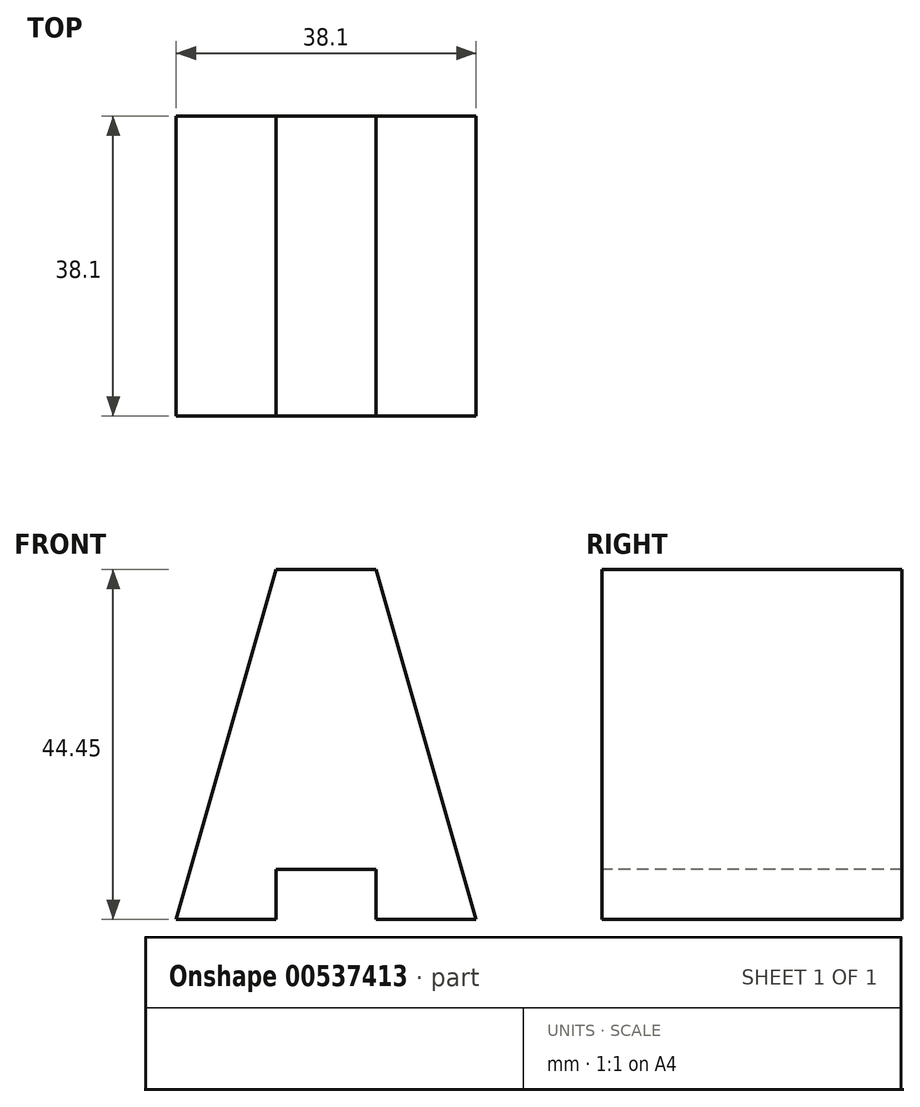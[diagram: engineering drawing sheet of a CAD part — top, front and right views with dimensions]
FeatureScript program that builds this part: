
annotation { "Feature Type Name" : "Feature", "Feature Type Description" : "" }
export const myFeature = defineFeature(function(context is Context, id is Id, definition is map)
    precondition{}
    {
        {
            var Q0;
            Q0=qCreatedBy(makeId("Front.planeOp"),FACE);
            var sketch = newSketch(context, id + "F0", { "sketchPlane" : qUnion([Q0])});
            skLineSegment(sketch, "E0", {"start": v(0, 0) * mm, "end": v(0, 44.45) * mm});
            skLineSegment(sketch, "E1", {"start": v(0, 44.45) * mm, "end": v(38.1, 44.45) * mm});
            skLineSegment(sketch, "E2", {"start": v(38.1, 44.45) * mm, "end": v(38.1, 0) * mm});
            skLineSegment(sketch, "E3", {"start": v(38.1, 0) * mm, "end": v(0, 0) * mm});
            skSolve(sketch);
        }
        {
            var Q0;
            Q0=makeQuery(id+"F0.imprint","IMPRINT",FACE,{"disambiguationData":[TD([[makeQuery(id+"F0.imprint","IMPRINT",EDGE,{"derivedFrom":sQuery(id+"F0.wireOp",EDGE,"E0")}),-1.0]])]});
            extrude(context, id + "F1", {"entities" : qUnion([Q0]), "depth" : 38.1 * mm, "offsetDistance" : 25.4 * mm});
        }
        {
            var Q0;
            Q0=makeQuery(id+"F1.opExtrude","CAP_FACE",FACE,{"disambiguationData":[OSD([sQuery(id+"F0.wireOp",EDGE,"E0"),sQuery(id+"F0.wireOp",EDGE,"E1"),sQuery(id+"F0.wireOp",EDGE,"E2"),sQuery(id+"F0.wireOp",EDGE,"E3")])],"isStart":false});
            var sketch = newSketch(context, id + "F2", { "sketchPlane" : qUnion([Q0])});
            skLineSegment(sketch, "E4", {"start": v(12.7, 0) * mm, "end": v(12.7, 44.45) * mm});
            skLineSegment(sketch, "E5", {"start": v(25.4, 0) * mm, "end": v(25.4, 44.45) * mm});
            skLineSegment(sketch, "E6", {"start": v(12.7, 6.35) * mm, "end": v(25.4, 6.35) * mm});
            skSolve(sketch);
        }
        {
            var Q0;
            {var subQ3=sQuery(id+"F2.wireOp",EDGE,"E6");Q0=makeQuery(id+"F2.imprint","IMPRINT",FACE,{"disambiguationData":[TD([[makeQuery(id+"F2.imprint","IMPRINT",EDGE,{"derivedFrom":subQ3}),-1.0]])]});}
            extrude(context, id + "F3", {"entities" : qUnion([Q0]), "operationType" : NewBodyOperationType.REMOVE, "oppositeDirection" : true, "depth" : 65.53 * mm, "offsetDistance" : 25.4 * mm});
        }
        {
            var Q0;
            Q0=makeQuery(id+"F1.opExtrude","CAP_FACE",FACE,{"disambiguationData":[OSD([sQuery(id+"F0.wireOp",EDGE,"E0"),sQuery(id+"F0.wireOp",EDGE,"E1"),sQuery(id+"F0.wireOp",EDGE,"E2"),sQuery(id+"F0.wireOp",EDGE,"E3")])],"isStart":false});
            var sketch = newSketch(context, id + "F4", { "sketchPlane" : qUnion([Q0])});
            skLineSegment(sketch, "E7", {"start": v(12.7, 44.45) * mm, "end": v(0, 0) * mm});
            skLineSegment(sketch, "E8", {"start": v(25.4, 44.45) * mm, "end": v(38.1, 0) * mm});
            skSolve(sketch);
        }
        {
            var Q0;
            {var subQ0=sQuery(id+"F4.wireOp",EDGE,"E7");Q0=makeQuery(id+"F4.imprint","IMPRINT",FACE,{"disambiguationData":[TD([[makeQuery(id+"F4.imprint","IMPRINT",EDGE,{"derivedFrom":subQ0}),-1.0]])]});}
            extrude(context, id + "F5", {"entities" : qUnion([Q0]), "operationType" : NewBodyOperationType.REMOVE, "oppositeDirection" : true, "depth" : 60.7 * mm, "offsetDistance" : 25.4 * mm});
        }
        {
            var Q0;
            Q0=makeQuery(id+"F1.opExtrude","CAP_FACE",FACE,{"disambiguationData":[OSD([sQuery(id+"F0.wireOp",EDGE,"E0"),sQuery(id+"F0.wireOp",EDGE,"E1"),sQuery(id+"F0.wireOp",EDGE,"E2"),sQuery(id+"F0.wireOp",EDGE,"E3")])],"isStart":false});
            var sketch = newSketch(context, id + "F6", { "sketchPlane" : qUnion([Q0])});
            skLineSegment(sketch, "E9", {"start": v(25.4, 44.45) * mm, "end": v(38.1, 0) * mm});
            skSolve(sketch);
        }
        {
            var Q0;
            {var subQ0=sQuery(id+"F6.wireOp",EDGE,"E9");Q0=makeQuery(id+"F6.imprint","IMPRINT",FACE,{"disambiguationData":[TD([[makeQuery(id+"F6.imprint","IMPRINT",EDGE,{"derivedFrom":subQ0}),1.0]])]});}
            extrude(context, id + "F7", {"entities" : qUnion([Q0]), "operationType" : NewBodyOperationType.REMOVE, "oppositeDirection" : true, "depth" : 60.7 * mm, "offsetDistance" : 25.4 * mm});
        }
    });
